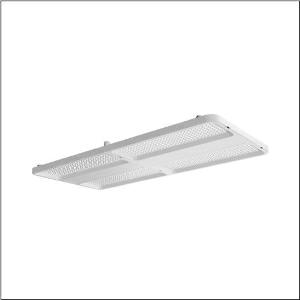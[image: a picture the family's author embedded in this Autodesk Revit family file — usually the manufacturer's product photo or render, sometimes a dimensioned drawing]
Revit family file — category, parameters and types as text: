
# Revit family: highbay_21_maxi_52hn11db3lda
name_source: partatom
category: Lighting Fixtures
units: mm (PartAtom-declared; Revit-internal decimal feet)

## family parameters
Cut with Voids When Loaded = No
Host = Face
Light Source = No
Part Type = Normal
Room Calculation Point = No
Round Connector Dimension = Use Diameter
Shared = No

## types (1)
- --- (1 x LED, 3880 lm, 22.6 W, 3000K)
    Apparent Load = 23 VA
    CIE Flux Codes = 89 97 99 100 100
    Color Rendering = 80
    Color Temperature = 3000K
    Default Elevation = 1800 mm
    Description = high bay luminaire Highbay 21 maxi; direct symmetric narrow distribution, light control with lens of PMMA; UGR ≤ 19 (X = 4H | Y = 8H | S = 0.25H | reflection values 70/50/20); luminous flux: 25.590lm; light colour: 830, colour temperature: 3000K, MacAdam ≤ 3 SDCM (initial), colour rendering: CRI > 80; luminous efficacy: 177,7lm/W; rated service life: 75.000h (L80) at AT= ta max; control: DALI 2; luminaire connection: terminal, 5-pole, max. 2.5mm² (cable entry for one cable, Ø 8.5..16mm); mains connection: 230..240V, AC/DC 0/50..60Hz; connected load: 144W; protection rating (complete): IP66; insulation class (complete): insulation class I (protective earthing); protection symbol: D; impact resistance: IK08; certification: CE, ENEC, VDE, UKCA; luminaire for central battery installations according to EN 60598-2-22, internal wiring halogen-free; luminaire LABS conformity tested according to VDMA 24364:2018-05; Suitable for use in the food industry according to the specifications of IFS-Food, HACCP and/or BRC; housing frame of high-performance plastic PA6, matt traffic white (RAL 9016); cover of PMMA; dimension (LxWxH): 946 x 442 x 72mm; permissible operating ambient temperature: -40..+65°C (reducing of maximum allowable ambient temperature of 5°C with ceiling mounting); packaging unit: 1 piece; (delivery without accessories; please order mounting accessories separately)
    Height = 72 mm  [stored 0.23622 ft]
    Lamp = 1 x LED
    Lamp Light Flux = 3880 lm
    Lamp Power = 22.6 W
    Lamp count = 1
    Length = 946 mm
    Luminous efficacy = 172 lm/W
    Manufacturer = Siteco
    ModVariant = No
    Model = 52HN11DB3LDA
    Mounting Place = Ceiling
    Mounting Type = Pendant
    Number of Poles = 1
    OnlyDefault = Yes
    Power Factor = 1
    Product Name = Highbay 21 maxi
    Product group = high bay luminaire
    ProductGroupID = 902
    Protection Class = Protection class I
    Protection Degree = IP 66
    RLX_Detail_Level = 1
    RLX_Emergency_Light_Flux = 0 lm
    RLX_Emergency_Type = 0
    RLX_Emergency_Type_DB = No
    RlxData = <blob elided: 127897 chars, md5=9fbdd00c>
    Socket = socket
    Standby Power = 0 W
    System Light Flux = 3880 lm
    System Power = 23 W
    Type Comments = : DC mode (central or group accumulator) initial emergency light level
    Type Image = l_1363244.jpg
    URL = http://relux.com
    VarID = @adj_003305
    Voltage = 0 V
    Weight = 0.00 kg
    Width = 442 mm

note: [stored X ft] marks values corroborated as IEEE doubles in the binary element streams (Revit-internal decimal feet)

## geometry (parser evidence)
native form markers: Blend x4, Sweep x10
no freeform markers — native parametric forms only
